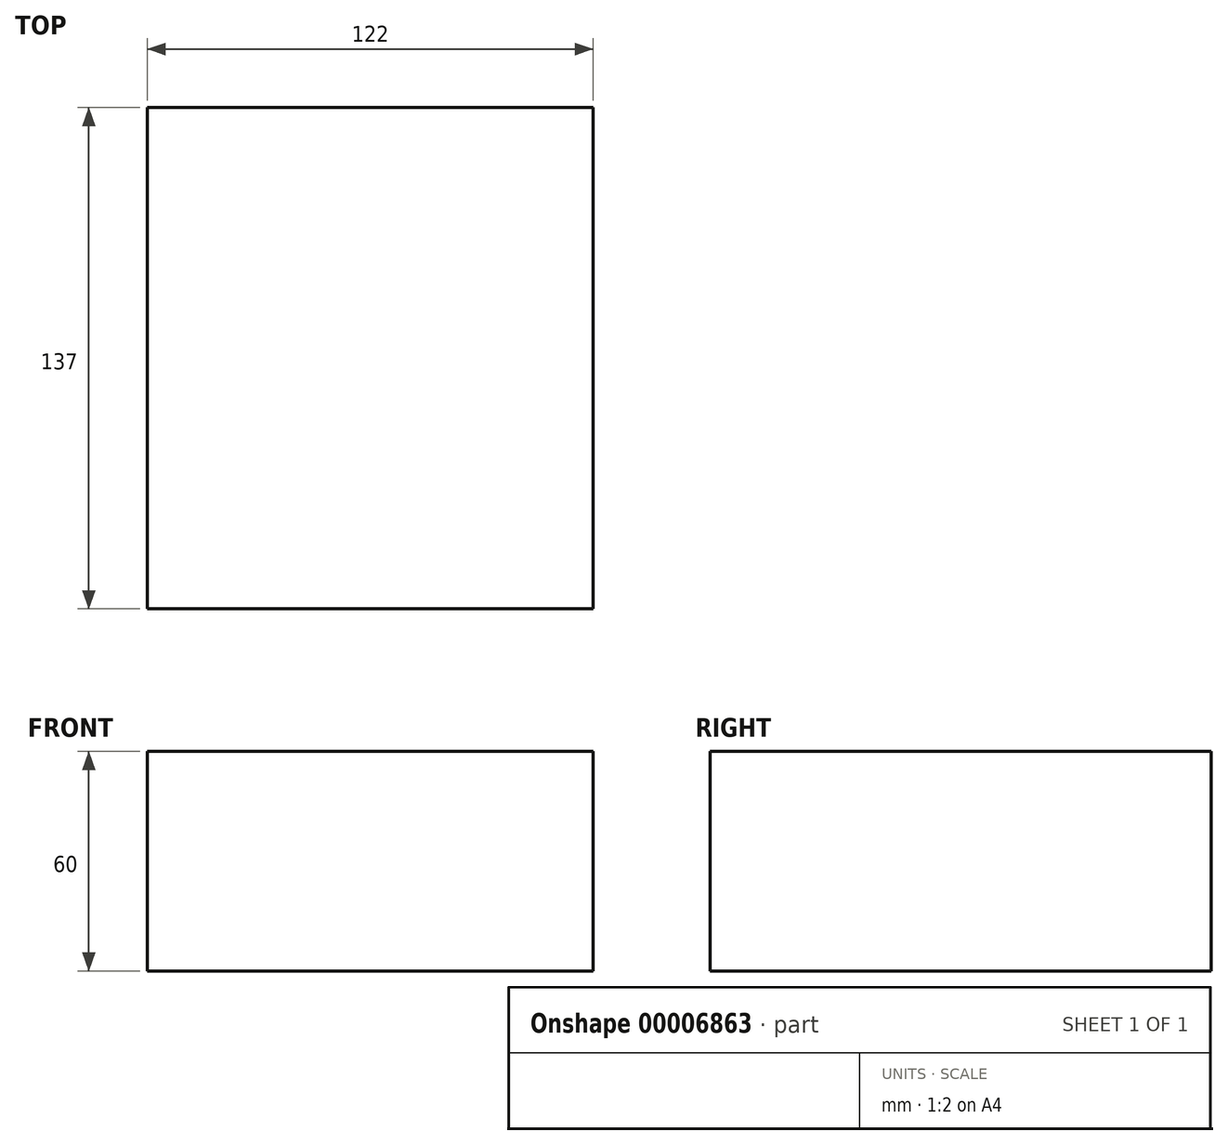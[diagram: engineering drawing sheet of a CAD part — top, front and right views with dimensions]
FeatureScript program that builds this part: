
annotation { "Feature Type Name" : "Feature", "Feature Type Description" : "" }
export const myFeature = defineFeature(function(context is Context, id is Id, definition is map)
    precondition{}
    {
        {
            var Q0;
            Q0=qCreatedBy(makeId("Top.planeOp"),FACE);
            var sketch = newSketch(context, id + "F0", { "sketchPlane" : qUnion([Q0])});
            skLineSegment(sketch, "E0.bottom", {"start": v(0, 0) * mm, "end": v(122, 0) * mm});
            skLineSegment(sketch, "E0.top", {"start": v(0, 137) * mm, "end": v(122, 137) * mm});
            skLineSegment(sketch, "E0.left", {"start": v(0, 0) * mm, "end": v(0, 137) * mm});
            skLineSegment(sketch, "E0.right", {"start": v(122, 0) * mm, "end": v(122, 137) * mm});
            skSolve(sketch);
        }
        {
            var Q0;
            Q0 = qSketchRegion(id + "F0", true);
            extrude(context, id + "F1", {"entities" : qUnion([Q0]), "depth" : 60 * mm});
        }
    });
